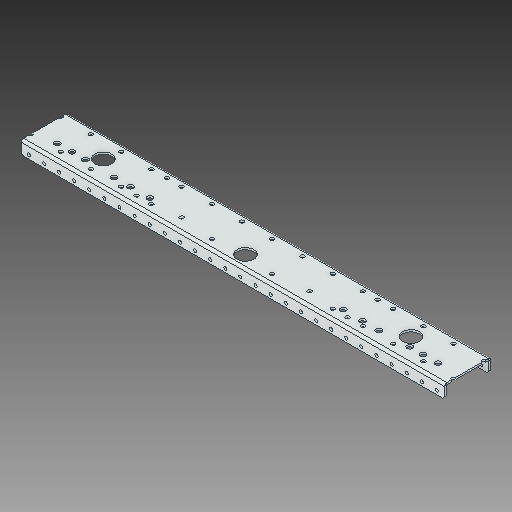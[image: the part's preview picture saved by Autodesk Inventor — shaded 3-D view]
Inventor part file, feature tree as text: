
AUTODESK INVENTOR PART (.ipt)
format: ipt  version: 2018 (Build 220112000, 112)  size: 219,136 bytes
history: native  units: in
note: dims shown in document units (in); Inventor stores cm internally (conversion verified against a paired STEP export)
features: chamfer x1
ambient origin geometry x8: Origin, YZ Plane, XZ Plane, XY Plane, X Axis, Y Axis, Z Axis, Center Point
bodies: Solid1 (feature_tree)
feature tree (1):
  chamfer  "Chamfer3"  [1 undecoded]
note: 1 required parameter value undecoded (feature->parameter linkage not recoverable at this tier; creation-order binding heuristic only, values carry confidence <= 0.55)
